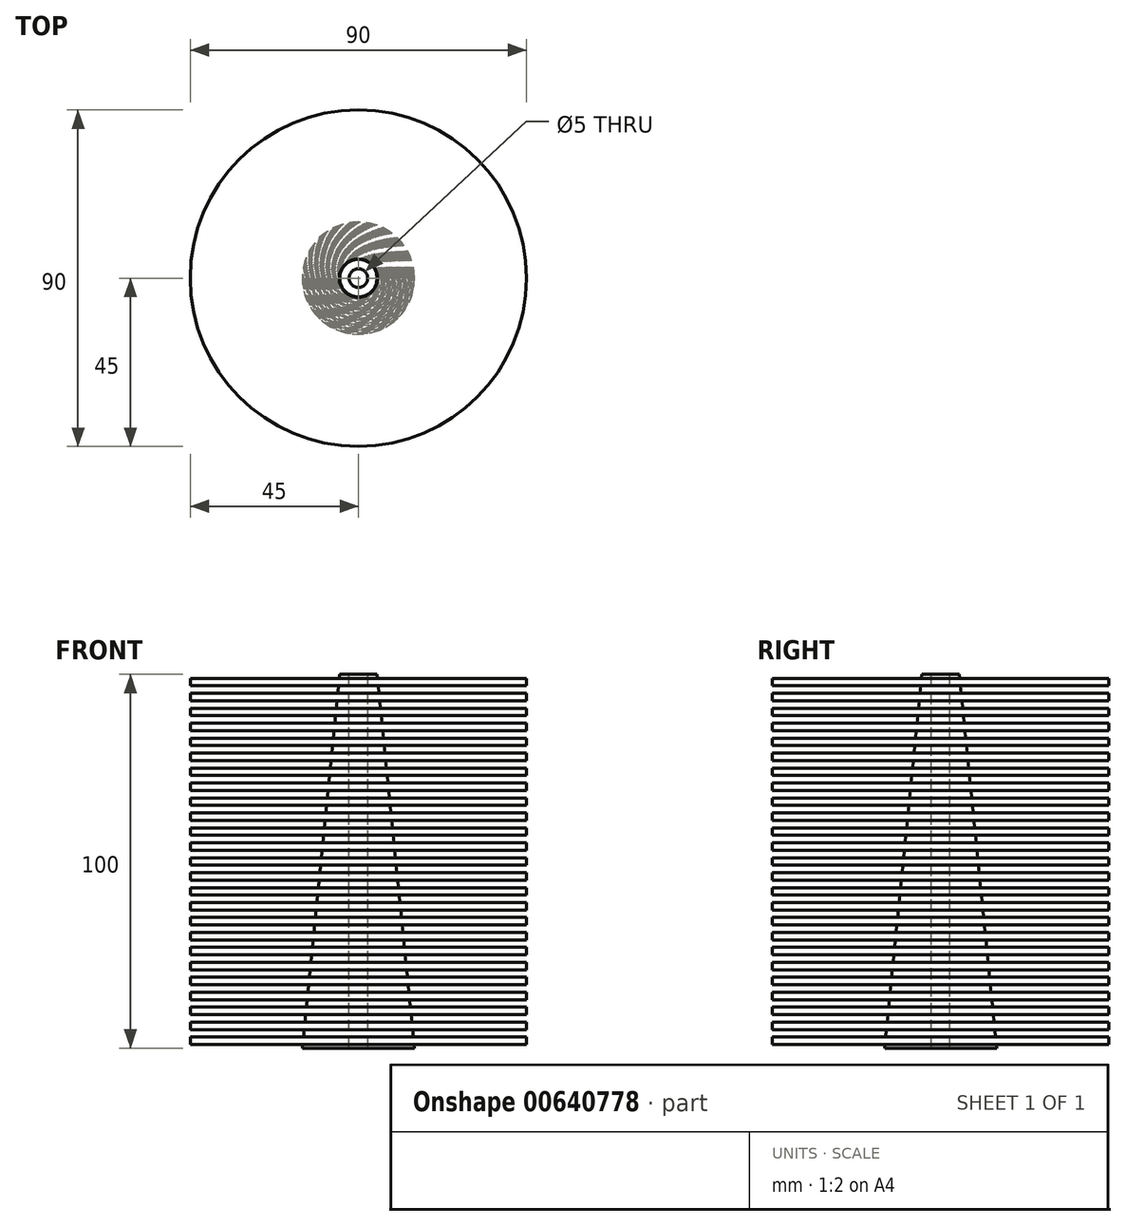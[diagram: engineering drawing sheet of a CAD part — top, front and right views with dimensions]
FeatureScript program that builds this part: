
annotation { "Feature Type Name" : "Feature", "Feature Type Description" : "" }
export const myFeature = defineFeature(function(context is Context, id is Id, definition is map)
    precondition{}
    {
        {
            var Q0;
            Q0=qCreatedBy(makeId("Front.planeOp"),FACE);
            var sketch = newSketch(context, id + "F0", { "sketchPlane" : qUnion([Q0])});
            skLineSegment(sketch, "E0", {"start": v(0, -49) * mm, "end": v(45, -49) * mm});
            skLineSegment(sketch, "E1", {"start": v(45, -49) * mm, "end": v(45, -47) * mm});
            skLineSegment(sketch, "E2", {"start": v(45, -47) * mm, "end": v(0, -47) * mm});
            skLineSegment(sketch, "E3", {"start": v(0, -47) * mm, "end": v(0, -49) * mm});
            skLineSegment(sketch, "E4.0.1.0", {"start": v(0, -45) * mm, "end": v(45, -45) * mm});
            skLineSegment(sketch, "E4.0.1.1", {"start": v(45, -43) * mm, "end": v(0, -43) * mm});
            skLineSegment(sketch, "E4.0.1.2", {"start": v(45, -45) * mm, "end": v(45, -43) * mm});
            skLineSegment(sketch, "E4.0.1.3", {"start": v(0, -43) * mm, "end": v(0, -45) * mm});
            skLineSegment(sketch, "E4.0.2.0", {"start": v(0, -41) * mm, "end": v(45, -41) * mm});
            skLineSegment(sketch, "E4.0.2.1", {"start": v(45, -39) * mm, "end": v(0, -39) * mm});
            skLineSegment(sketch, "E4.0.2.2", {"start": v(45, -41) * mm, "end": v(45, -39) * mm});
            skLineSegment(sketch, "E4.0.2.3", {"start": v(0, -39) * mm, "end": v(0, -41) * mm});
            skLineSegment(sketch, "E4.0.3.0", {"start": v(0, -37) * mm, "end": v(45, -37) * mm});
            skLineSegment(sketch, "E4.0.3.1", {"start": v(45, -35) * mm, "end": v(0, -35) * mm});
            skLineSegment(sketch, "E4.0.3.2", {"start": v(45, -37) * mm, "end": v(45, -35) * mm});
            skLineSegment(sketch, "E4.0.3.3", {"start": v(0, -35) * mm, "end": v(0, -37) * mm});
            skLineSegment(sketch, "E4.0.4.0", {"start": v(0, -33) * mm, "end": v(45, -33) * mm});
            skLineSegment(sketch, "E4.0.4.1", {"start": v(45, -31) * mm, "end": v(0, -31) * mm});
            skLineSegment(sketch, "E4.0.4.2", {"start": v(45, -33) * mm, "end": v(45, -31) * mm});
            skLineSegment(sketch, "E4.0.4.3", {"start": v(0, -31) * mm, "end": v(0, -33) * mm});
            skLineSegment(sketch, "E4.0.5.0", {"start": v(0, -29) * mm, "end": v(45, -29) * mm});
            skLineSegment(sketch, "E4.0.5.1", {"start": v(45, -27) * mm, "end": v(0, -27) * mm});
            skLineSegment(sketch, "E4.0.5.2", {"start": v(45, -29) * mm, "end": v(45, -27) * mm});
            skLineSegment(sketch, "E4.0.5.3", {"start": v(0, -27) * mm, "end": v(0, -29) * mm});
            skLineSegment(sketch, "E4.0.6.0", {"start": v(0, -25) * mm, "end": v(45, -25) * mm});
            skLineSegment(sketch, "E4.0.6.1", {"start": v(45, -23) * mm, "end": v(0, -23) * mm});
            skLineSegment(sketch, "E4.0.6.2", {"start": v(45, -25) * mm, "end": v(45, -23) * mm});
            skLineSegment(sketch, "E4.0.6.3", {"start": v(0, -23) * mm, "end": v(0, -25) * mm});
            skLineSegment(sketch, "E4.0.7.0", {"start": v(0, -21) * mm, "end": v(45, -21) * mm});
            skLineSegment(sketch, "E4.0.7.1", {"start": v(45, -19) * mm, "end": v(0, -19) * mm});
            skLineSegment(sketch, "E4.0.7.2", {"start": v(45, -21) * mm, "end": v(45, -19) * mm});
            skLineSegment(sketch, "E4.0.7.3", {"start": v(0, -19) * mm, "end": v(0, -21) * mm});
            skLineSegment(sketch, "E4.0.8.0", {"start": v(0, -17) * mm, "end": v(45, -17) * mm});
            skLineSegment(sketch, "E4.0.8.1", {"start": v(45, -15) * mm, "end": v(0, -15) * mm});
            skLineSegment(sketch, "E4.0.8.2", {"start": v(45, -17) * mm, "end": v(45, -15) * mm});
            skLineSegment(sketch, "E4.0.8.3", {"start": v(0, -15) * mm, "end": v(0, -17) * mm});
            skLineSegment(sketch, "E4.0.9.0", {"start": v(0, -13) * mm, "end": v(45, -13) * mm});
            skLineSegment(sketch, "E4.0.9.1", {"start": v(45, -11) * mm, "end": v(0, -11) * mm});
            skLineSegment(sketch, "E4.0.9.2", {"start": v(45, -13) * mm, "end": v(45, -11) * mm});
            skLineSegment(sketch, "E4.0.9.3", {"start": v(0, -11) * mm, "end": v(0, -13) * mm});
            skLineSegment(sketch, "E4.0.10.0", {"start": v(0, -9) * mm, "end": v(45, -9) * mm});
            skLineSegment(sketch, "E4.0.10.1", {"start": v(45, -7) * mm, "end": v(0, -7) * mm});
            skLineSegment(sketch, "E4.0.10.2", {"start": v(45, -9) * mm, "end": v(45, -7) * mm});
            skLineSegment(sketch, "E4.0.10.3", {"start": v(0, -7) * mm, "end": v(0, -9) * mm});
            skLineSegment(sketch, "E4.0.11.0", {"start": v(0, -5) * mm, "end": v(45, -5) * mm});
            skLineSegment(sketch, "E4.0.11.1", {"start": v(45, -3) * mm, "end": v(0, -3) * mm});
            skLineSegment(sketch, "E4.0.11.2", {"start": v(45, -5) * mm, "end": v(45, -3) * mm});
            skLineSegment(sketch, "E4.0.11.3", {"start": v(0, -3) * mm, "end": v(0, -5) * mm});
            skLineSegment(sketch, "E4.0.12.0", {"start": v(0, -1) * mm, "end": v(45, -1) * mm});
            skLineSegment(sketch, "E4.0.12.1", {"start": v(45, 1) * mm, "end": v(0, 1) * mm});
            skLineSegment(sketch, "E4.0.12.2", {"start": v(45, -1) * mm, "end": v(45, 1) * mm});
            skLineSegment(sketch, "E4.0.12.3", {"start": v(0, 1) * mm, "end": v(0, -1) * mm});
            skLineSegment(sketch, "E4.0.13.0", {"start": v(0, 3) * mm, "end": v(45, 3) * mm});
            skLineSegment(sketch, "E4.0.13.1", {"start": v(45, 5) * mm, "end": v(0, 5) * mm});
            skLineSegment(sketch, "E4.0.13.2", {"start": v(45, 3) * mm, "end": v(45, 5) * mm});
            skLineSegment(sketch, "E4.0.13.3", {"start": v(0, 5) * mm, "end": v(0, 3) * mm});
            skLineSegment(sketch, "E4.0.14.0", {"start": v(0, 7) * mm, "end": v(45, 7) * mm});
            skLineSegment(sketch, "E4.0.14.1", {"start": v(45, 9) * mm, "end": v(0, 9) * mm});
            skLineSegment(sketch, "E4.0.14.2", {"start": v(45, 7) * mm, "end": v(45, 9) * mm});
            skLineSegment(sketch, "E4.0.14.3", {"start": v(0, 9) * mm, "end": v(0, 7) * mm});
            skLineSegment(sketch, "E4.0.15.0", {"start": v(0, 11) * mm, "end": v(45, 11) * mm});
            skLineSegment(sketch, "E4.0.15.1", {"start": v(45, 13) * mm, "end": v(0, 13) * mm});
            skLineSegment(sketch, "E4.0.15.2", {"start": v(45, 11) * mm, "end": v(45, 13) * mm});
            skLineSegment(sketch, "E4.0.15.3", {"start": v(0, 13) * mm, "end": v(0, 11) * mm});
            skLineSegment(sketch, "E4.0.16.0", {"start": v(0, 15) * mm, "end": v(45, 15) * mm});
            skLineSegment(sketch, "E4.0.16.1", {"start": v(45, 17) * mm, "end": v(0, 17) * mm});
            skLineSegment(sketch, "E4.0.16.2", {"start": v(45, 15) * mm, "end": v(45, 17) * mm});
            skLineSegment(sketch, "E4.0.16.3", {"start": v(0, 17) * mm, "end": v(0, 15) * mm});
            skLineSegment(sketch, "E4.0.17.0", {"start": v(0, 19) * mm, "end": v(45, 19) * mm});
            skLineSegment(sketch, "E4.0.17.1", {"start": v(45, 21) * mm, "end": v(0, 21) * mm});
            skLineSegment(sketch, "E4.0.17.2", {"start": v(45, 19) * mm, "end": v(45, 21) * mm});
            skLineSegment(sketch, "E4.0.17.3", {"start": v(0, 21) * mm, "end": v(0, 19) * mm});
            skLineSegment(sketch, "E4.0.18.0", {"start": v(0, 23) * mm, "end": v(45, 23) * mm});
            skLineSegment(sketch, "E4.0.18.1", {"start": v(45, 25) * mm, "end": v(0, 25) * mm});
            skLineSegment(sketch, "E4.0.18.2", {"start": v(45, 23) * mm, "end": v(45, 25) * mm});
            skLineSegment(sketch, "E4.0.18.3", {"start": v(0, 25) * mm, "end": v(0, 23) * mm});
            skLineSegment(sketch, "E4.0.19.0", {"start": v(0, 27) * mm, "end": v(45, 27) * mm});
            skLineSegment(sketch, "E4.0.19.1", {"start": v(45, 29) * mm, "end": v(0, 29) * mm});
            skLineSegment(sketch, "E4.0.19.2", {"start": v(45, 27) * mm, "end": v(45, 29) * mm});
            skLineSegment(sketch, "E4.0.19.3", {"start": v(0, 29) * mm, "end": v(0, 27) * mm});
            skLineSegment(sketch, "E4.0.20.0", {"start": v(0, 31) * mm, "end": v(45, 31) * mm});
            skLineSegment(sketch, "E4.0.20.1", {"start": v(45, 33) * mm, "end": v(0, 33) * mm});
            skLineSegment(sketch, "E4.0.20.2", {"start": v(45, 31) * mm, "end": v(45, 33) * mm});
            skLineSegment(sketch, "E4.0.20.3", {"start": v(0, 33) * mm, "end": v(0, 31) * mm});
            skLineSegment(sketch, "E4.0.21.0", {"start": v(0, 35) * mm, "end": v(45, 35) * mm});
            skLineSegment(sketch, "E4.0.21.1", {"start": v(45, 37) * mm, "end": v(0, 37) * mm});
            skLineSegment(sketch, "E4.0.21.2", {"start": v(45, 35) * mm, "end": v(45, 37) * mm});
            skLineSegment(sketch, "E4.0.21.3", {"start": v(0, 37) * mm, "end": v(0, 35) * mm});
            skLineSegment(sketch, "E4.0.22.0", {"start": v(0, 39) * mm, "end": v(45, 39) * mm});
            skLineSegment(sketch, "E4.0.22.1", {"start": v(45, 41) * mm, "end": v(0, 41) * mm});
            skLineSegment(sketch, "E4.0.22.2", {"start": v(45, 39) * mm, "end": v(45, 41) * mm});
            skLineSegment(sketch, "E4.0.22.3", {"start": v(0, 41) * mm, "end": v(0, 39) * mm});
            skLineSegment(sketch, "E4.0.23.0", {"start": v(0, 43) * mm, "end": v(45, 43) * mm});
            skLineSegment(sketch, "E4.0.23.1", {"start": v(45, 45) * mm, "end": v(0, 45) * mm});
            skLineSegment(sketch, "E4.0.23.2", {"start": v(45, 43) * mm, "end": v(45, 45) * mm});
            skLineSegment(sketch, "E4.0.23.3", {"start": v(0, 45) * mm, "end": v(0, 43) * mm});
            skLineSegment(sketch, "E4.0.24.0", {"start": v(0, 47) * mm, "end": v(45, 47) * mm});
            skLineSegment(sketch, "E4.0.24.1", {"start": v(45, 49) * mm, "end": v(0, 49) * mm});
            skLineSegment(sketch, "E4.0.24.2", {"start": v(45, 47) * mm, "end": v(45, 49) * mm});
            skLineSegment(sketch, "E4.0.24.3", {"start": v(0, 49) * mm, "end": v(0, 47) * mm});
            skLineSegment(sketch, "E4.direction1", {"start": v(0, -49) * mm, "end": v(45, -49.04) * mm, "construction": true});
            skLineSegment(sketch, "E4.direction2", {"start": v(0, -49) * mm, "end": v(0, -45) * mm, "construction": true});
            skLineSegment(sketch, "E5", {"start": v(0, 49) * mm, "end": v(0, -49) * mm});
            skSolve(sketch);
        }
        {
            var Q0;
            Q0=qCreatedBy(makeId("Top.planeOp"),FACE);
            var sketch = newSketch(context, id + "F1", { "sketchPlane" : qUnion([Q0])});
            skCircle(sketch, "E6", {"center": v(0, 0) * mm, "radius": 2.5 * mm});
            skCircle(sketch, "E7", {"center": v(0, 0) * mm, "radius": 2.15 * mm});
            skSolve(sketch);
        }
        {
            var Q0;
            Q0 = qSketchRegion(id + "F1", true);
            extrude(context, id + "F2", {"entities" : qUnion([Q0]), "depth" : 50 * mm, "offsetDistance" : 25 * mm, "hasSecondDirection" : true, "secondDirectionOppositeDirection" : true, "secondDirectionDepth" : 50 * mm});
        }
        {
            var Q0;
            {var subQ0=sQuery(id+"F0.wireOp",EDGE,"E4.0.8.0");Q0=makeQuery(id+"F0.imprint","IMPRINT",FACE,{"disambiguationData":[TD([[makeQuery(id+"F0.imprint","IMPRINT",EDGE,{"derivedFrom":subQ0}),1.0]])]});}
            var Q1;
            {var subQ0=sQuery(id+"F0.wireOp",EDGE,"E4.0.23.0");Q1=makeQuery(id+"F0.imprint","IMPRINT",FACE,{"disambiguationData":[TD([[makeQuery(id+"F0.imprint","IMPRINT",EDGE,{"derivedFrom":subQ0}),1.0]])]});}
            var Q2;
            {var subQ0=sQuery(id+"F0.wireOp",EDGE,"E4.0.9.0");Q2=makeQuery(id+"F0.imprint","IMPRINT",FACE,{"disambiguationData":[TD([[makeQuery(id+"F0.imprint","IMPRINT",EDGE,{"derivedFrom":subQ0}),1.0]])]});}
            var Q3;
            {var subQ0=sQuery(id+"F0.wireOp",EDGE,"E4.0.4.0");Q3=makeQuery(id+"F0.imprint","IMPRINT",FACE,{"disambiguationData":[TD([[makeQuery(id+"F0.imprint","IMPRINT",EDGE,{"derivedFrom":subQ0}),1.0]])]});}
            var Q4;
            {var subQ0=sQuery(id+"F0.wireOp",EDGE,"E4.0.3.0");Q4=makeQuery(id+"F0.imprint","IMPRINT",FACE,{"disambiguationData":[TD([[makeQuery(id+"F0.imprint","IMPRINT",EDGE,{"derivedFrom":subQ0}),1.0]])]});}
            var Q5;
            {var subQ0=sQuery(id+"F0.wireOp",EDGE,"E4.0.1.0");Q5=makeQuery(id+"F0.imprint","IMPRINT",FACE,{"disambiguationData":[TD([[makeQuery(id+"F0.imprint","IMPRINT",EDGE,{"derivedFrom":subQ0}),1.0]])]});}
            var Q6;
            {var subQ0=sQuery(id+"F0.wireOp",EDGE,"E4.0.15.0");Q6=makeQuery(id+"F0.imprint","IMPRINT",FACE,{"disambiguationData":[TD([[makeQuery(id+"F0.imprint","IMPRINT",EDGE,{"derivedFrom":subQ0}),1.0]])]});}
            var Q7;
            {var subQ0=sQuery(id+"F0.wireOp",EDGE,"E4.0.20.0");Q7=makeQuery(id+"F0.imprint","IMPRINT",FACE,{"disambiguationData":[TD([[makeQuery(id+"F0.imprint","IMPRINT",EDGE,{"derivedFrom":subQ0}),1.0]])]});}
            var Q8;
            {var subQ0=sQuery(id+"F0.wireOp",EDGE,"E4.0.22.0");Q8=makeQuery(id+"F0.imprint","IMPRINT",FACE,{"disambiguationData":[TD([[makeQuery(id+"F0.imprint","IMPRINT",EDGE,{"derivedFrom":subQ0}),1.0]])]});}
            var Q9;
            {var subQ0=sQuery(id+"F0.wireOp",EDGE,"E4.0.18.0");Q9=makeQuery(id+"F0.imprint","IMPRINT",FACE,{"disambiguationData":[TD([[makeQuery(id+"F0.imprint","IMPRINT",EDGE,{"derivedFrom":subQ0}),1.0]])]});}
            var Q10;
            {var subQ0=sQuery(id+"F0.wireOp",EDGE,"E4.0.19.0");Q10=makeQuery(id+"F0.imprint","IMPRINT",FACE,{"disambiguationData":[TD([[makeQuery(id+"F0.imprint","IMPRINT",EDGE,{"derivedFrom":subQ0}),1.0]])]});}
            var Q11;
            {var subQ0=sQuery(id+"F0.wireOp",EDGE,"E4.0.13.0");Q11=makeQuery(id+"F0.imprint","IMPRINT",FACE,{"disambiguationData":[TD([[makeQuery(id+"F0.imprint","IMPRINT",EDGE,{"derivedFrom":subQ0}),1.0]])]});}
            var Q12;
            {var subQ0=sQuery(id+"F0.wireOp",EDGE,"E4.0.16.0");Q12=makeQuery(id+"F0.imprint","IMPRINT",FACE,{"disambiguationData":[TD([[makeQuery(id+"F0.imprint","IMPRINT",EDGE,{"derivedFrom":subQ0}),1.0]])]});}
            var Q13;
            {var subQ0=sQuery(id+"F0.wireOp",EDGE,"E4.0.14.0");Q13=makeQuery(id+"F0.imprint","IMPRINT",FACE,{"disambiguationData":[TD([[makeQuery(id+"F0.imprint","IMPRINT",EDGE,{"derivedFrom":subQ0}),1.0]])]});}
            var Q14;
            {var subQ0=sQuery(id+"F0.wireOp",EDGE,"E4.0.5.0");Q14=makeQuery(id+"F0.imprint","IMPRINT",FACE,{"disambiguationData":[TD([[makeQuery(id+"F0.imprint","IMPRINT",EDGE,{"derivedFrom":subQ0}),1.0]])]});}
            var Q15;
            {var subQ0=sQuery(id+"F0.wireOp",EDGE,"E4.0.6.0");Q15=makeQuery(id+"F0.imprint","IMPRINT",FACE,{"disambiguationData":[TD([[makeQuery(id+"F0.imprint","IMPRINT",EDGE,{"derivedFrom":subQ0}),1.0]])]});}
            var Q16;
            {var subQ0=sQuery(id+"F0.wireOp",EDGE,"E4.0.7.0");Q16=makeQuery(id+"F0.imprint","IMPRINT",FACE,{"disambiguationData":[TD([[makeQuery(id+"F0.imprint","IMPRINT",EDGE,{"derivedFrom":subQ0}),1.0]])]});}
            var Q17;
            {var subQ0=sQuery(id+"F0.wireOp",EDGE,"E4.0.10.0");Q17=makeQuery(id+"F0.imprint","IMPRINT",FACE,{"disambiguationData":[TD([[makeQuery(id+"F0.imprint","IMPRINT",EDGE,{"derivedFrom":subQ0}),1.0]])]});}
            var Q18;
            {var subQ0=sQuery(id+"F0.wireOp",EDGE,"E4.0.11.0");Q18=makeQuery(id+"F0.imprint","IMPRINT",FACE,{"disambiguationData":[TD([[makeQuery(id+"F0.imprint","IMPRINT",EDGE,{"derivedFrom":subQ0}),1.0]])]});}
            var Q19;
            {var subQ0=sQuery(id+"F0.wireOp",EDGE,"E4.0.17.0");Q19=makeQuery(id+"F0.imprint","IMPRINT",FACE,{"disambiguationData":[TD([[makeQuery(id+"F0.imprint","IMPRINT",EDGE,{"derivedFrom":subQ0}),1.0]])]});}
            var Q20;
            {var subQ0=sQuery(id+"F0.wireOp",EDGE,"E4.0.21.0");Q20=makeQuery(id+"F0.imprint","IMPRINT",FACE,{"disambiguationData":[TD([[makeQuery(id+"F0.imprint","IMPRINT",EDGE,{"derivedFrom":subQ0}),1.0]])]});}
            var Q21;
            {var subQ0=sQuery(id+"F0.wireOp",EDGE,"E4.0.2.0");Q21=makeQuery(id+"F0.imprint","IMPRINT",FACE,{"disambiguationData":[TD([[makeQuery(id+"F0.imprint","IMPRINT",EDGE,{"derivedFrom":subQ0}),1.0]])]});}
            var Q22;
            {var subQ0=sQuery(id+"F0.wireOp",EDGE,"E0");Q22=makeQuery(id+"F0.imprint","IMPRINT",FACE,{"disambiguationData":[TD([[makeQuery(id+"F0.imprint","IMPRINT",EDGE,{"derivedFrom":subQ0}),1.0]])]});}
            var Q23;
            {var subQ0=sQuery(id+"F0.wireOp",EDGE,"E4.0.24.0");Q23=makeQuery(id+"F0.imprint","IMPRINT",FACE,{"disambiguationData":[TD([[makeQuery(id+"F0.imprint","IMPRINT",EDGE,{"derivedFrom":subQ0}),1.0]])]});}
            var Q24;
            {var subQ0=sQuery(id+"F0.wireOp",EDGE,"E4.0.12.0");Q24=makeQuery(id+"F0.imprint","IMPRINT",FACE,{"disambiguationData":[TD([[makeQuery(id+"F0.imprint","IMPRINT",EDGE,{"derivedFrom":subQ0}),1.0]])]});}
            var Q25;
            Q25=sQuery(id+"F0.wireOp",EDGE,"E5");
            revolve(context, id + "F3", {"operationType" : NewBodyOperationType.ADD, "entities" : qUnion([Q0, Q1, Q2, Q3, Q4, Q5, Q6, Q7, Q8, Q9, Q10, Q11, Q12, Q13, Q14, Q15, Q16, Q17, Q18, Q19, Q20, Q21, Q22, Q23, Q24]), "axis" : qUnion([Q25]), "revolveType" : RevolveType.FULL});
        }
        {
            var Q0;
            Q0=qCreatedBy(makeId("Front.planeOp"),FACE);
            var sketch = newSketch(context, id + "F4", { "sketchPlane" : qUnion([Q0])});
            skLineSegment(sketch, "E8", {"start": v(0, 50.06) * mm, "end": v(0, -49.94) * mm});
            skLineSegment(sketch, "E9", {"start": v(0, -49.94) * mm, "end": v(15, -49.94) * mm});
            skLineSegment(sketch, "E10", {"start": v(15, -49.94) * mm, "end": v(5, 50.06) * mm});
            skLineSegment(sketch, "E11", {"start": v(5, 50.06) * mm, "end": v(0, 50.06) * mm});
            skSolve(sketch);
        }
        {
            var Q0;
            Q0 = qSketchRegion(id + "F4", true);
            var Q1;
            Q1=sQuery(id+"F4.wireOp",EDGE,"E8");
            revolve(context, id + "F5", {"operationType" : NewBodyOperationType.ADD, "entities" : qUnion([Q0]), "axis" : qUnion([Q1]), "revolveType" : RevolveType.FULL, "oppositeDirection" : true});
        }
        {
            var Q0;
            Q0 = qSketchRegion(id + "F1", true);
            var Q1;
            Q1=sQuery(id+"F1.wireOp",EDGE,"E7");
            extrude(context, id + "F6", {"entities" : qUnion([Q0]), "operationType" : NewBodyOperationType.REMOVE, "surfaceEntities" : qUnion([Q1]), "endBound" : BoundingType.THROUGH_ALL, "oppositeDirection" : true, "depth" : 25 * mm, "offsetDistance" : 25 * mm, "hasSecondDirection" : true, "secondDirectionBound" : BoundingType.THROUGH_ALL, "secondDirectionOppositeDirection" : false, "secondDirectionDepth" : 25 * mm});
        }
        {
            var Q0;
            Q0=makeQuery(id+"F6.boolean.opBoolean","SPLIT",FACE,{"disambiguationData":[TD([makeQuery(id+"F6.opExtrude","SWEPT_FACE",FACE,{"disambiguationData":[OSD([sQuery(id+"F1.wireOp",EDGE,"E7")])]})])],"derivedFrom":makeQuery(id+"F5.opRevolve","SWEPT_FACE",FACE,{"disambiguationData":[OSD([sQuery(id+"F4.wireOp",EDGE,"E11")])]})});
            extrude(context, id + "F7", {"entities" : qUnion([Q0]), "operationType" : NewBodyOperationType.REMOVE, "endBound" : BoundingType.THROUGH_ALL, "oppositeDirection" : true, "depth" : 25 * mm, "offsetDistance" : 25 * mm});
        }
    });
